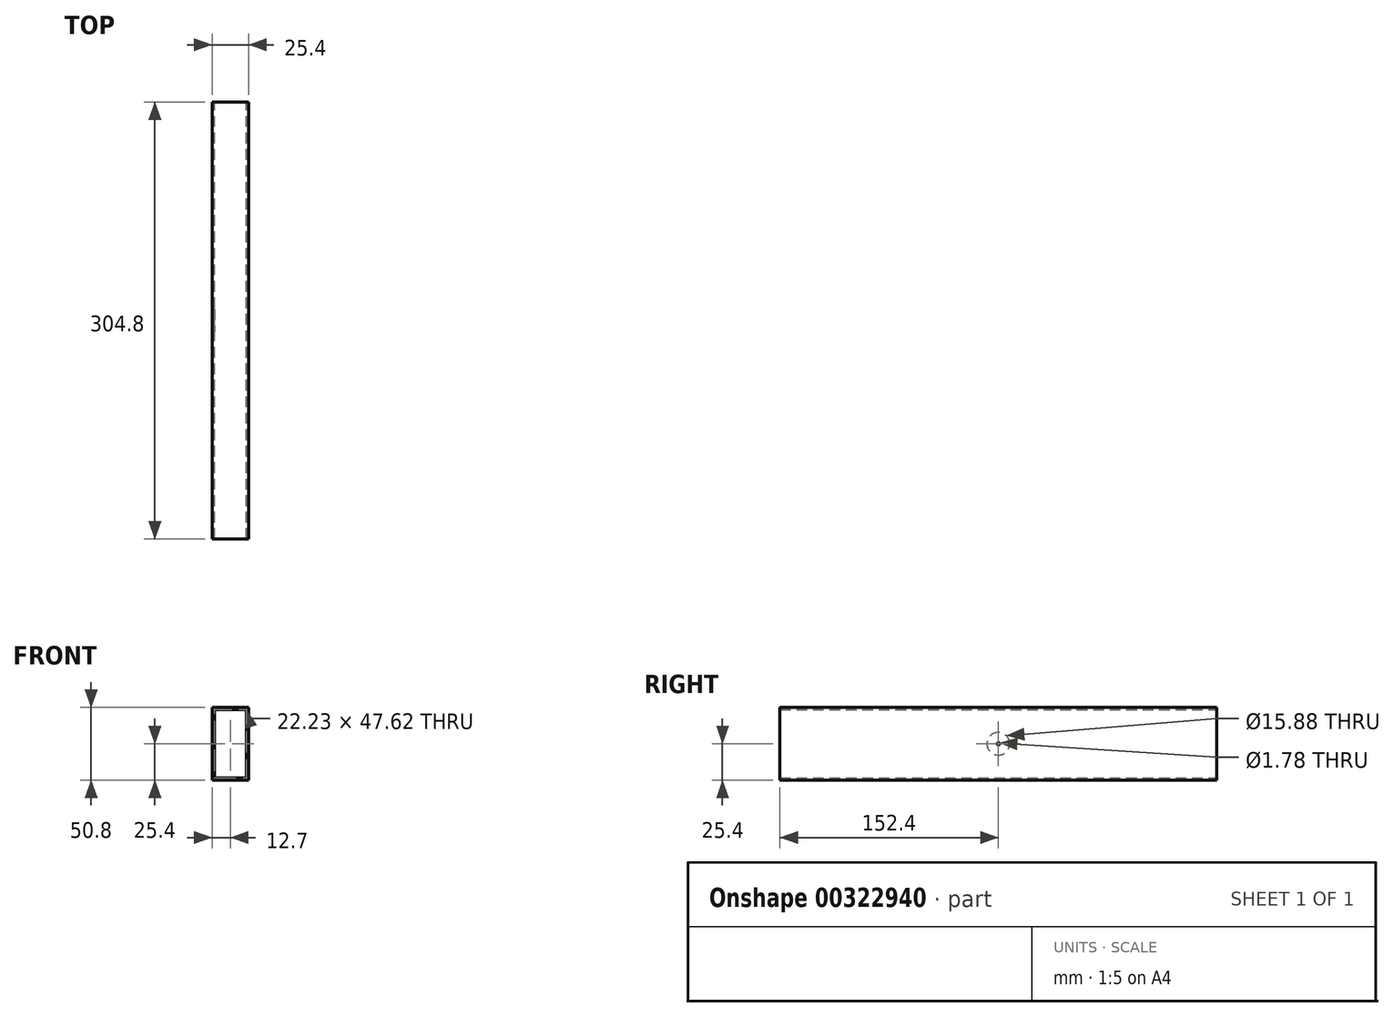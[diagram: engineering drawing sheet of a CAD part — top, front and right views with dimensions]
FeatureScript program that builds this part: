
annotation { "Feature Type Name" : "Feature", "Feature Type Description" : "" }
export const myFeature = defineFeature(function(context is Context, id is Id, definition is map)
    precondition{}
    {
        {
            var Q0;
            Q0=qCreatedBy(makeId("Front.planeOp"),FACE);
            var sketch = newSketch(context, id + "F0", { "sketchPlane" : qUnion([Q0])});
            skLineSegment(sketch, "E0.bottom", {"start": v(-12.7, 25.4) * mm, "end": v(12.7, 25.4) * mm});
            skLineSegment(sketch, "E0.top", {"start": v(-12.7, -25.4) * mm, "end": v(12.7, -25.4) * mm});
            skLineSegment(sketch, "E0.left", {"start": v(-12.7, 25.4) * mm, "end": v(-12.7, -25.4) * mm});
            skLineSegment(sketch, "E0.right", {"start": v(12.7, 25.4) * mm, "end": v(12.7, -25.4) * mm});
            skPoint(sketch, "E0.middle", {"position": v(0, 0) * mm});
            skLineSegment(sketch, "E1.bottom", {"start": v(-11.11, 23.81) * mm, "end": v(11.11, 23.81) * mm});
            skLineSegment(sketch, "E1.top", {"start": v(-11.11, -23.81) * mm, "end": v(11.11, -23.81) * mm});
            skLineSegment(sketch, "E1.left", {"start": v(-11.11, 23.81) * mm, "end": v(-11.11, -23.81) * mm});
            skLineSegment(sketch, "E1.right", {"start": v(11.11, 23.81) * mm, "end": v(11.11, -23.81) * mm});
            skSolve(sketch);
        }
        {
            var Q0;
            Q0=makeQuery(id+"F0.imprint","IMPRINT",FACE,{"disambiguationData":[TD([[makeQuery(id+"F0.imprint","IMPRINT",EDGE,{"derivedFrom":sQuery(id+"F0.wireOp",EDGE,"E0.bottom")}),-1.0]])]});
            extrude(context, id + "F1", {"entities" : qUnion([Q0]), "depth" : 304.8 * mm});
        }
        {
            var Q0;
            Q0=makeQuery(id+"F1.opExtrude","SWEPT_FACE",FACE,{"disambiguationData":[OSD([sQuery(id+"F0.wireOp",EDGE,"E0.left")])]});
            var sketch = newSketch(context, id + "F2", { "sketchPlane" : qUnion([Q0])});
            skCircle(sketch, "E2", {"center": v(152.4, 0) * mm, "radius": 7.94 * mm});
            skSolve(sketch);
        }
        {
            var Q0;
            Q0 = qSketchRegion(id + "F2", true);
            extrude(context, id + "F3", {"entities" : qUnion([Q0]), "operationType" : NewBodyOperationType.REMOVE, "oppositeDirection" : true, "depth" : 1.59 * mm});
        }
        {
            var Q0;
            Q0=makeQuery(id+"F1.opExtrude","SWEPT_FACE",FACE,{"disambiguationData":[OSD([sQuery(id+"F0.wireOp",EDGE,"E0.right")])]});
            var sketch = newSketch(context, id + "F4", { "sketchPlane" : qUnion([Q0])});
            skCircle(sketch, "E3", {"center": v(-152.4, 0) * mm, "radius": 0.89 * mm});
            skSolve(sketch);
        }
        {
            var Q0;
            Q0 = qSketchRegion(id + "F4", true);
            extrude(context, id + "F5", {"entities" : qUnion([Q0]), "operationType" : NewBodyOperationType.REMOVE, "oppositeDirection" : true, "depth" : 1.59 * mm});
        }
    });
